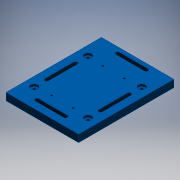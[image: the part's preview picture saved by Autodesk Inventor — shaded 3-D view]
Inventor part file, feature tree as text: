
AUTODESK INVENTOR PART (.ipt)
format: ipt  version: 2016 (Build 200138000, 138)  size: 205,312 bytes
history: native  units: mm
features: sketch x4, extrude x2, hole x2
ambient origin geometry x8: Origin, YZ Plane, XZ Plane, XY Plane, X Axis, Y Axis, Z Axis, Center Point
bodies: Solid1 (feature_tree)
feature tree (8):
  extrude  "flash4base"  Depth=10.0mm
  hole  "flash4mountingholes"  [1 undecoded]
  hole  "mountinPostMountingHoles"  [1 undecoded]
  extrude  "m6Alignment"  Depth=143.4mm
  sketch  "Sketch2"  dims[d9=120.0mm d10=125.0mm d11=7.0mm d12=4.0mm d13=10.0mm d16=125.0mm]
  sketch  "Sketch3"  dims[d17=62.5mm d18=85.0mm]
  sketch  "Sketch4"  dims[d19=42.5mm d20=25.0mm]
  sketch  "Sketch5"  dims[d21=25.0mm d23=22.5mm d24=13.5mm d25=0.0mm d26=40.0mm d27=20.0mm d28=95.3mm d29=47.65mm d30=3.4mm d31=6.0mm d32=11.0mm d33=2.6mm d34=14.3117mm d35=8.0mm d36=20.594885mm d37=100.0mm d38=50.0mm d39=100.0mm d40=4.5mm d41=6.0mm d42=13.0mm d43=3.4mm d44=14.3117mm d45=8.0mm d46=20.594885mm d48=6.6mm d50=6.6mm d52=30.0mm d53=30.0mm d54=30.0mm d55=30.0mm d56=50.0mm d57=2.0mm d58=3.0mm d59=3.0mm d60=10.0mm d61=0.0mm d62=6.6mm d63=6.6mm d64=30.0mm d65=30.0mm d66=30.0mm d67=30.0mm d70=3.0mm d71=93.4mm d72=46.7mm d73=143.4mm d74=65.0mm d75=30.0mm]
note: 2 required parameter values undecoded (feature->parameter linkage not recoverable at this tier; creation-order binding heuristic only, values carry confidence <= 0.55)
